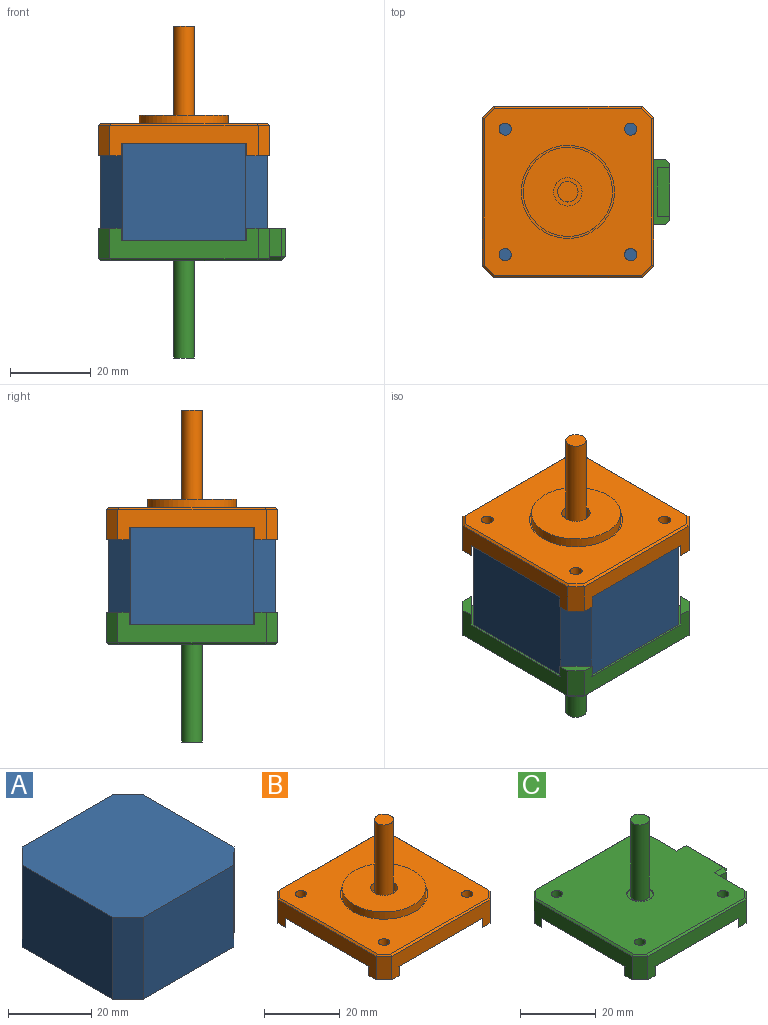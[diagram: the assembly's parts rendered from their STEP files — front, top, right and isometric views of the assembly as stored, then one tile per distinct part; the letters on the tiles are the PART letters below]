
ASSEMBLY  parts=3 mates=2
PART A: 10 faces, bbox 41.3x41.3x24 mm
  f0: plane 30.57x24mm, normal (0,1,0), area 733.7mm2, adj f1,f7,f8,f9
  f1: plane 24x5.36mm, normal (-0.71,0.71,0), area 182.1mm2, adj f0,f2,f8,f9
  f2: plane 30.57x24mm, normal (-1,0,0), area 733.7mm2, adj f1,f3,f8,f9
  f3: plane 24x5.36mm, normal (-0.71,-0.71,0), area 182.1mm2, adj f2,f4,f8,f9
  f4: plane 30.57x24mm, normal (0,-1,0), area 733.7mm2, adj f3,f5,f8,f9
  f5: plane 24x5.36mm, normal (0.71,-0.71,0), area 182.1mm2, adj f4,f6,f8,f9
  f6: plane 30.57x24mm, normal (1,0,0), area 733.7mm2, adj f5,f7,f8,f9
  f7: plane 24x5.36mm, normal (0.71,0.71,0), area 182.1mm2, adj f0,f6,f8,f9
  f8: plane 41.3x41.3mm, normal (0,0,1), area 1648.1mm2, adj f0,f1,f2,f3,f4,f5,f6,f7
  f9: plane 41.3x41.3mm, normal (0,0,-1), area 1648.1mm2, adj f0,f1,f2,f3,f4,f5,f6,f7
PART B: 38 faces, bbox 42.3x42.3x32 mm
  f0: plane 36.64x7.5mm, normal (-1,0,0), area 181.9mm2, adj f1,f10,f13,f14,f15,f20,f21,f32
  f1: plane 7.5x2.83mm, normal (-0.71,-0.71,0), area 30mm2, adj f0,f2,f15,f34
  f2: plane 36.64x7.5mm, normal (0,-1,0), area 181.9mm2, adj f1,f3,f13,f14,f15,f16,f17,f36
  f3: plane 7.5x2.83mm, normal (0.71,-0.71,0), area 30mm2, adj f2,f4,f17,f37
  f4: plane 36.64x7.5mm, normal (1,0,0), area 181.9mm2, adj f3,f5,f13,f16,f17,f18,f19,f35
  f5: plane 7.5x2.83mm, normal (0.71,0.71,0), area 30mm2, adj f4,f6,f19,f33
  f6: plane 36.64x7.5mm, normal (0,1,0), area 181.9mm2, adj f5,f10,f13,f18,f19,f20,f21,f31
  f7: cylinder r=1.5mm len=5mm, axis (0,0,-1), area 47.1mm2, adj f12,f13
  f8: cylinder r=1.5mm len=5mm, axis (0,0,-1), area 47.1mm2, adj f12,f13
  f9: cylinder r=1.5mm len=5mm, axis (0,0,-1), area 47.1mm2, adj f12,f13
  f10: plane 7.5x2.83mm, normal (-0.71,0.71,0), area 30mm2, adj f0,f6,f21,f30
  f11: cylinder r=1.5mm len=5mm, axis (0,0,-1), area 47.1mm2, adj f12,f13
  f12: plane 41.3x41.3mm, normal (0,0,1), area 1249.1mm2, adj f7,f8,f9,f11,f23,f30,f31,f32
  f13: plane 42.3x42.3mm, normal (0,0,-1), area 1697mm2, adj f0,f2,f4,f6,f7,f8,f9,f11
  f14: plane 5.66x5.66mm, normal (0.71,0.71,0), area 24mm2, adj f0,f2,f13,f15
  f15: plane 5.66x5.66mm, normal (0,0,-1), area 12mm2, adj f0,f1,f2,f14
  f16: plane 5.66x5.66mm, normal (-0.71,0.71,0), area 24mm2, adj f2,f4,f13,f17
  f17: plane 5.66x5.66mm, normal (0,0,-1), area 12mm2, adj f2,f3,f4,f16
  f18: plane 5.66x5.66mm, normal (-0.71,-0.71,0), area 24mm2, adj f4,f6,f13,f19
  f19: plane 5.66x5.66mm, normal (0,0,-1), area 12mm2, adj f4,f5,f6,f18
  f20: plane 5.66x5.66mm, normal (0.71,-0.71,0), area 24mm2, adj f0,f6,f13,f21
  f21: plane 5.66x5.66mm, normal (0,0,-1), area 12mm2, adj f0,f6,f10,f20
  f22: cylinder r=11mm len=22mm, axis (0,0,-1), area 172.8mm2, adj f24,f25
  f23: cylinder r=11.5mm len=23mm, axis (0,0,-1), area 36.1mm2, adj f12,f24
  f24: plane 23x23mm, normal (0,0,1), area 35.3mm2, adj f22,f23
  f25: plane 22x22mm, normal (0,0,1), area 341.6mm2, adj f22,f27
  f26: cylinder r=2.5mm len=24.5mm, axis (0,0,-1), area 384.8mm2, adj f28,f29
  f27: cylinder r=3.5mm len=7mm, axis (0,0,-1), area 55mm2, adj f25,f28
  f28: plane 7x7mm, normal (0,0,1), area 18.8mm2, adj f26,f27
  f29: plane 5x5mm, normal (0,0,1), area 19.6mm2, adj f26
  f30: plane 3.04x3.04mm, normal (-0.5,0.5,0.71), area 2.7mm2, adj f10,f12,f31,f32
  f31: plane 36.64x0.5mm, normal (0,0.71,0.71), area 25.8mm2, adj f6,f12,f30,f33
  f32: plane 36.64x0.5mm, normal (-0.71,0,0.71), area 25.8mm2, adj f0,f12,f30,f34
  f33: plane 3.04x3.04mm, normal (0.5,0.5,0.71), area 2.7mm2, adj f5,f12,f31,f35
  f34: plane 3.04x3.04mm, normal (-0.5,-0.5,0.71), area 2.7mm2, adj f1,f12,f32,f36
  f35: plane 36.64x0.5mm, normal (0.71,0,0.71), area 25.8mm2, adj f4,f12,f33,f37
  f36: plane 36.64x0.5mm, normal (0,-0.71,0.71), area 25.8mm2, adj f2,f12,f34,f37
  f37: plane 3.04x3.04mm, normal (0.5,-0.5,0.71), area 2.7mm2, adj f3,f12,f35,f36
PART C: 52 faces, bbox 46.3x42.3x32 mm
  f0: plane 42.3x42.3mm, normal (0,0,-1), area 1697mm2, adj f1,f5,f7,f9,f11,f12,f13,f14
  f1: plane 10.82x7.5mm, normal (1,0,0), area 55.1mm2, adj f0,f2,f15,f29,f30,f35,f51
  f2: plane 7x3mm, normal (0,-1,0), area 21mm2, adj f1,f25,f28,f35,f38
  f3: plane 14x7mm, normal (1,0,0), area 38mm2, adj f24,f26,f28,f31,f33,f36,f38
  f4: plane 7x3mm, normal (0,1,0), area 21mm2, adj f5,f25,f28,f32,f33
  f5: plane 10.82x7.5mm, normal (1,0,0), area 55.1mm2, adj f0,f4,f6,f22,f23,f32,f43
  f6: plane 7.5x2.83mm, normal (0.71,0.71,0), area 30mm2, adj f5,f7,f23,f44
  f7: plane 36.64x7.5mm, normal (0,1,0), area 181.9mm2, adj f0,f6,f8,f20,f21,f22,f23,f45
  f8: plane 7.5x2.83mm, normal (-0.71,0.71,0), area 30mm2, adj f7,f9,f21,f46
  f9: plane 36.64x7.5mm, normal (-1,0,0), area 181.9mm2, adj f0,f8,f10,f18,f19,f20,f21,f47
  f10: plane 7.5x2.83mm, normal (-0.71,-0.71,0), area 30mm2, adj f9,f11,f19,f48
  f11: plane 36.64x7.5mm, normal (0,-1,0), area 181.9mm2, adj f0,f10,f15,f18,f19,f29,f30,f49
  f12: cylinder r=1.5mm len=5mm, axis (0,0,-1), area 47.1mm2, adj f0,f17
  f13: cylinder r=1.5mm len=5mm, axis (0,0,-1), area 47.1mm2, adj f0,f17
  f14: cylinder r=1.5mm len=5mm, axis (0,0,-1), area 47.1mm2, adj f0,f17
  f15: plane 7.5x2.83mm, normal (0.71,-0.71,0), area 30mm2, adj f1,f11,f30,f50
  f16: cylinder r=1.5mm len=5mm, axis (0,0,-1), area 47.1mm2, adj f0,f17
  f17: plane 44.8x41.3mm, normal (0,0,1), area 1675.1mm2, adj f12,f13,f14,f16,f32,f35,f36,f40
  f18: plane 5.66x5.66mm, normal (0.71,0.71,0), area 24mm2, adj f0,f9,f11,f19
  f19: plane 5.66x5.66mm, normal (0,0,-1), area 12mm2, adj f9,f10,f11,f18
  f20: plane 5.66x5.66mm, normal (0.71,-0.71,0), area 24mm2, adj f0,f7,f9,f21
  f21: plane 5.66x5.66mm, normal (0,0,-1), area 12mm2, adj f7,f8,f9,f20
  f22: plane 5.66x5.66mm, normal (-0.71,-0.71,0), area 24mm2, adj f0,f5,f7,f23
  f23: plane 5.66x5.66mm, normal (0,0,-1), area 12mm2, adj f5,f6,f7,f22
  f24: plane 5x3mm, normal (0,-1,0), area 15mm2, adj f3,f27,f28,f31
  f25: plane 16x3mm, normal (-1,0,0), area 48mm2, adj f0,f2,f4,f28
  f26: plane 5x3mm, normal (0,1,0), area 15mm2, adj f3,f27,f28,f31
  f27: plane 12x5mm, normal (1,0,0), area 60mm2, adj f24,f26,f28,f31
  f28: plane 16x4mm, normal (0,0,-1), area 27mm2, adj f2,f3,f4,f24,f25,f26,f27,f33
  f29: plane 5.66x5.66mm, normal (-0.71,0.71,0), area 24mm2, adj f0,f1,f11,f30
  f30: plane 5.66x5.66mm, normal (0,0,-1), area 12mm2, adj f1,f11,f15,f29
  f31: plane 12x3mm, normal (0,0,-1), area 36mm2, adj f3,f24,f26,f27
  f32: plane 3.5x1mm, normal (0,0.71,0.71), area 4.4mm2, adj f4,f5,f17,f34,f43
  f33: plane 7x1mm, normal (0.71,0.71,0), area 9.9mm2, adj f3,f4,f28,f34
  f34: plane 1x1mm, normal (0.58,0.58,0.58), area 0.9mm2, adj f32,f33,f36
  f35: plane 3.5x1mm, normal (0,-0.71,0.71), area 4.4mm2, adj f1,f2,f17,f37,f51
  f36: plane 14x1mm, normal (0.71,0,0.71), area 19.8mm2, adj f3,f17,f34,f37
  f37: plane 1x1mm, normal (0.58,-0.58,0.58), area 0.9mm2, adj f35,f36,f38
  f38: plane 7x1mm, normal (0.71,-0.71,0), area 9.9mm2, adj f2,f3,f28,f37
  f39: cylinder r=2.5mm len=24.5mm, axis (0,0,-1), area 384.8mm2, adj f41,f42
  f40: cylinder r=3.5mm len=7mm, axis (0,0,-1), area 11mm2, adj f17,f41
  f41: plane 7x7mm, normal (0,0,1), area 18.8mm2, adj f39,f40
  f42: plane 5x5mm, normal (0,0,1), area 19.6mm2, adj f39
  f43: plane 11.32x0.5mm, normal (0.71,0,0.71), area 7.8mm2, adj f5,f17,f32,f44
  f44: plane 3.04x3.04mm, normal (0.5,0.5,0.71), area 2.7mm2, adj f6,f17,f43,f45
  f45: plane 36.64x0.5mm, normal (0,0.71,0.71), area 25.8mm2, adj f7,f17,f44,f46
  f46: plane 3.04x3.04mm, normal (-0.5,0.5,0.71), area 2.7mm2, adj f8,f17,f45,f47
  f47: plane 36.64x0.5mm, normal (-0.71,0,0.71), area 25.8mm2, adj f9,f17,f46,f48
  f48: plane 3.04x3.04mm, normal (-0.5,-0.5,0.71), area 2.7mm2, adj f10,f17,f47,f49
  f49: plane 36.64x0.5mm, normal (0,-0.71,0.71), area 25.8mm2, adj f11,f17,f48,f50
  f50: plane 3.04x3.04mm, normal (0.5,-0.5,0.71), area 2.7mm2, adj f15,f17,f49,f51
  f51: plane 11.32x0.5mm, normal (0.71,0,0.71), area 7.8mm2, adj f1,f17,f35,f50
PLACE A t=(-62.3,-42.3,-24)mm
PLACE B at identity fixed
PLACE C rot(axis=(1,0,0),180deg) t=(0,52.3,-24)mm
MATE fastened C.f39 <-> A.f9  axis (0,0,1) through (0,0,-24)mm
MATE fastened B.f23 <-> A.f8  axis (0,0,-1) through (0,0,0)mm
